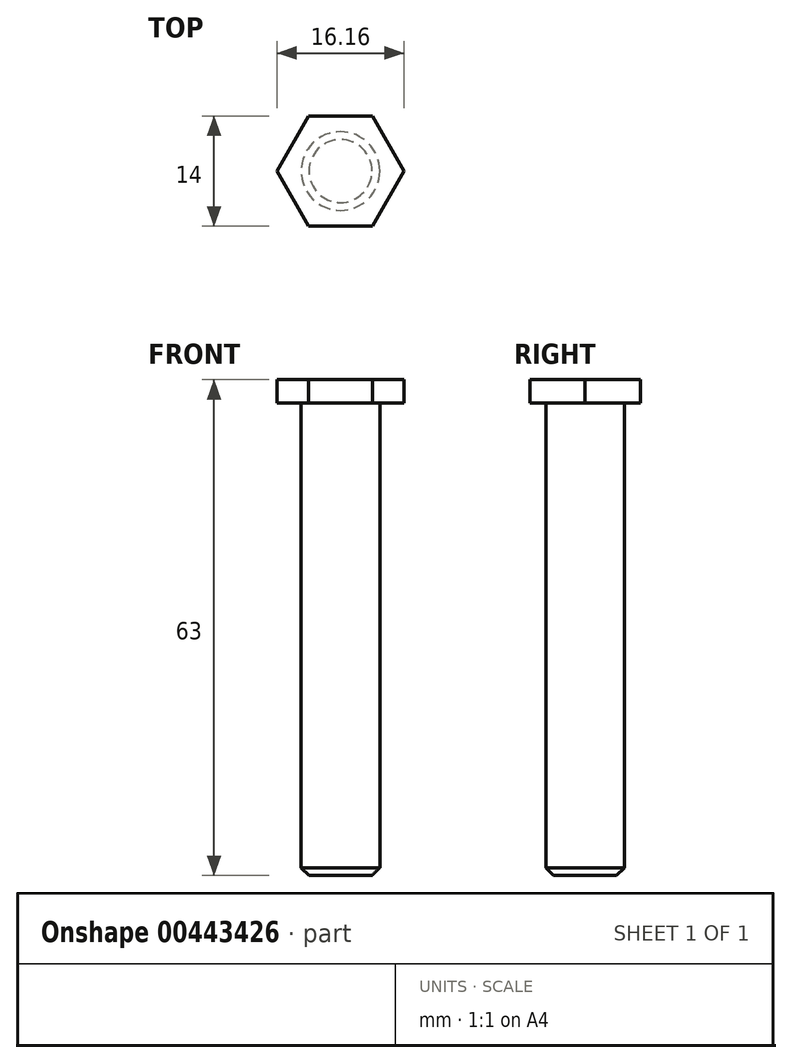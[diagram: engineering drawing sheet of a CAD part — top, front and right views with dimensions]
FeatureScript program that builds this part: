
annotation { "Feature Type Name" : "Feature", "Feature Type Description" : "" }
export const myFeature = defineFeature(function(context is Context, id is Id, definition is map)
    precondition{}
    {
        {
            var Q0;
            Q0=qCreatedBy(makeId("Top.planeOp"),FACE);
            var sketch = newSketch(context, id + "F0", { "sketchPlane" : qUnion([Q0])});
            skCircle(sketch, "E0", {"center": v(0, 0) * mm, "radius": 5 * mm});
            skSolve(sketch);
        }
        {
            var Q0;
            Q0=makeQuery(id+"F0.imprint","IMPRINT",FACE,{"disambiguationData":[TD([[makeQuery(id+"F0.imprint","IMPRINT",EDGE,{"derivedFrom":sQuery(id+"F0.wireOp",EDGE,"E0")}),1.0]])]});
            extrude(context, id + "F1", {"entities" : qUnion([Q0]), "depth" : 60 * mm});
        }
        {
            var Q0;
            Q0=makeQuery(id+"F1.opExtrude","CAP_EDGE",EDGE,{"disambiguationData":[OSD([sQuery(id+"F0.wireOp",EDGE,"E0")])],"isStart":true});
            chamfer(context, id + "F2", {"entities" : qUnion([Q0]), "chamferType" : ChamferType.OFFSET_ANGLE, "width" : 1 * mm, "oppositeDirection" : false, "angle" : 45 * degree, "tangentPropagation" : true});
        }
        {
            var Q0;
            Q0=makeQuery(id+"F1.opExtrude","CAP_FACE",FACE,{"disambiguationData":[OSD([sQuery(id+"F0.wireOp",EDGE,"E0")])],"isStart":false});
            var sketch = newSketch(context, id + "F3", { "sketchPlane" : qUnion([Q0])});
            skCircle(sketch, "E1.cCircle", {"center": v(0, 0) * mm, "radius": 7 * mm, "construction": true});
            skLineSegment(sketch, "E1.0", {"start": v(4.04, 7) * mm, "end": v(8.08, 0) * mm});
            skLineSegment(sketch, "E1.1", {"start": v(8.08, 0) * mm, "end": v(4.04, -7) * mm});
            skLineSegment(sketch, "E1.2", {"start": v(4.04, -7) * mm, "end": v(-4.04, -7) * mm});
            skLineSegment(sketch, "E1.3", {"start": v(-4.04, -7) * mm, "end": v(-8.08, 0) * mm});
            skLineSegment(sketch, "E1.4", {"start": v(-8.08, 0) * mm, "end": v(-4.04, 7) * mm});
            skLineSegment(sketch, "E1.5", {"start": v(-4.04, 7) * mm, "end": v(4.04, 7) * mm});
            skPoint(sketch, "E1.0.midPoint", {"position": v(6.06, 3.5) * mm});
            skSolve(sketch);
        }
        {
            var Q0;
            Q0=qSketchRegion(id+"F3",true);
            extrude(context, id + "F4", {"entities" : qUnion([Q0]), "operationType" : NewBodyOperationType.ADD, "depth" : 3 * mm});
        }
    });
